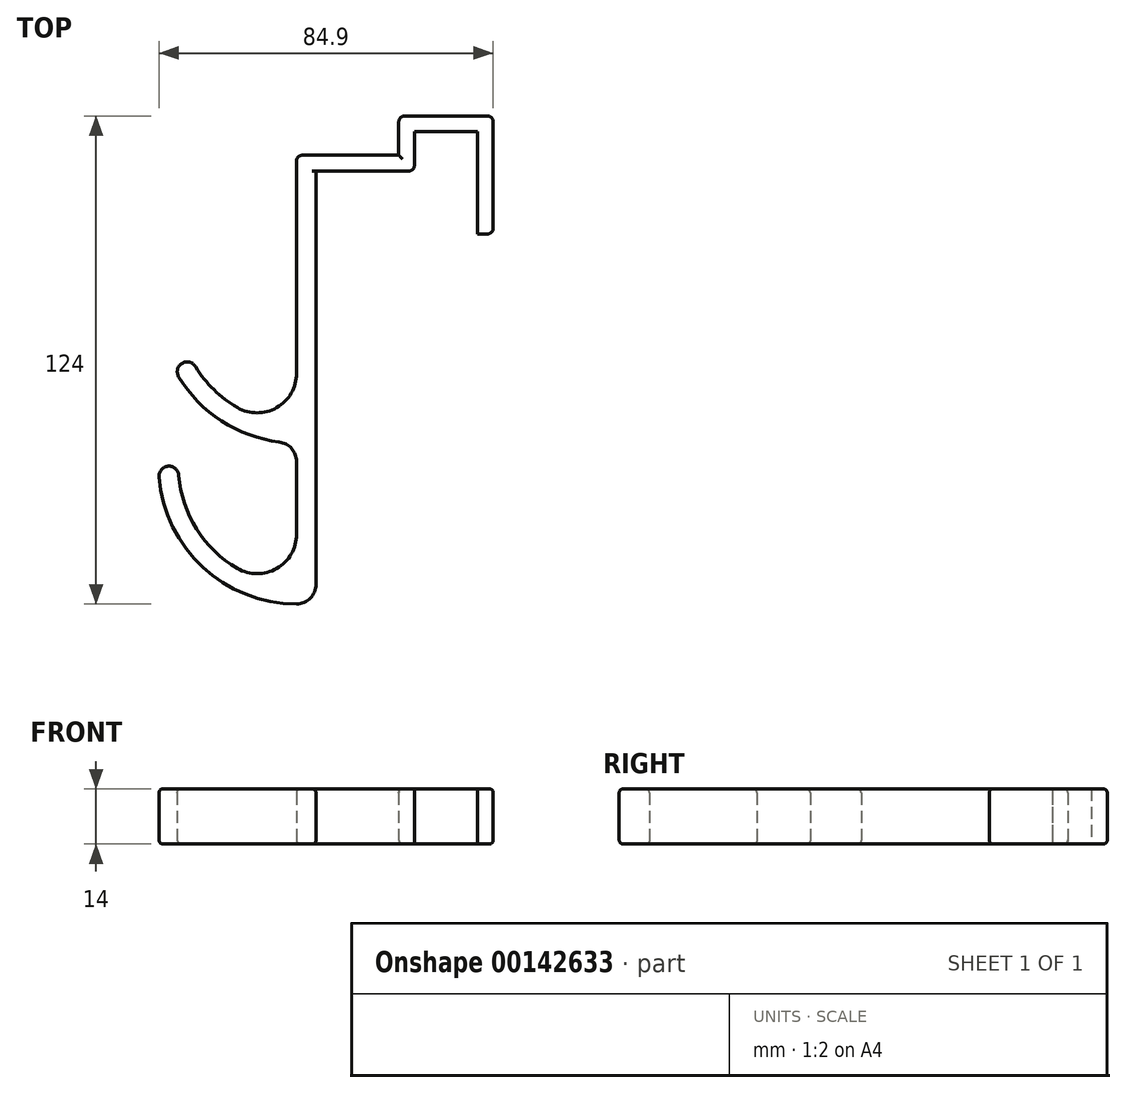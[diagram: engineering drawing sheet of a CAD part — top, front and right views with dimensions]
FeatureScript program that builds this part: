
annotation { "Feature Type Name" : "Feature", "Feature Type Description" : "" }
export const myFeature = defineFeature(function(context is Context, id is Id, definition is map)
    precondition{}
    {
        {
            var Q0;
            Q0=qCreatedBy(makeId("Top.planeOp"),FACE);
            var sketch = newSketch(context, id + "F0", { "sketchPlane" : qUnion([Q0])});
            skLineSegment(sketch, "E0", {"start": v(45, -14.5) * mm, "end": v(45, 12.5) * mm});
            skLineSegment(sketch, "E1", {"start": v(43.5, 14) * mm, "end": v(22.5, 14) * mm});
            skLineSegment(sketch, "E2", {"start": v(21, 12.5) * mm, "end": v(21, 4) * mm});
            skLineSegment(sketch, "E3", {"start": v(21, 4) * mm, "end": v(-3.5, 4) * mm});
            skLineSegment(sketch, "E4", {"start": v(-5, 2.5) * mm, "end": v(-5, -51.45) * mm});
            skLineSegment(sketch, "E5", {"start": v(-37.4, -75) * mm, "end": v(-37.4, -75) * mm});
            skLineSegment(sketch, "E6", {"start": v(-5, -110) * mm, "end": v(-5, -110) * mm});
            skLineSegment(sketch, "E7", {"start": v(0, 0) * mm, "end": v(23.5, 0) * mm});
            skLineSegment(sketch, "E8", {"start": v(25, 1.5) * mm, "end": v(25, 10) * mm});
            skLineSegment(sketch, "E9", {"start": v(25, 10) * mm, "end": v(41, 10) * mm});
            skLineSegment(sketch, "E10", {"start": v(41, 10) * mm, "end": v(41, -16) * mm});
            skLineSegment(sketch, "E11", {"start": v(41, -16) * mm, "end": v(43.5, -16) * mm});
            skLineSegment(sketch, "E12.trimOffspring", {"start": v(0, -105) * mm, "end": v(0, 0) * mm});
            skArc(sketch, "E13", {"start": v(-34.91, -77.3) * mm, "mid": v(-30.38, -90.99) * mm, "end": v(-20, -100.98) * mm});
            skArc(sketch, "E14", {"start": v(-39.9, -77.7) * mm, "mid": v(-28.78, -100.68) * mm, "end": v(-5, -110) * mm});
            skPoint(sketch, "E15.visualSharp", {"position": v(-35, -75) * mm});
            skArc(sketch, "E15.filletArc", {"start": v(-34.91, -77.3) * mm, "mid": v(-35.7, -75.67) * mm, "end": v(-37.4, -75) * mm});
            skPoint(sketch, "E16.visualSharp", {"position": v(-40, -75) * mm});
            skArc(sketch, "E16.filletArc", {"start": v(-37.4, -75) * mm, "mid": v(-39.24, -75.8) * mm, "end": v(-39.9, -77.7) * mm});
            skPoint(sketch, "E17.visualSharp", {"position": v(-5, 4) * mm});
            skArc(sketch, "E17.filletArc", {"start": v(-3.5, 4) * mm, "mid": v(-4.56, 3.56) * mm, "end": v(-5, 2.5) * mm});
            skPoint(sketch, "E18.visualSharp", {"position": v(25, 0) * mm});
            skArc(sketch, "E18.filletArc", {"start": v(23.5, 0) * mm, "mid": v(24.56, 0.44) * mm, "end": v(25, 1.5) * mm});
            skPoint(sketch, "E19.visualSharp", {"position": v(21, 14) * mm});
            skArc(sketch, "E19.filletArc", {"start": v(22.5, 14) * mm, "mid": v(21.44, 13.56) * mm, "end": v(21, 12.5) * mm});
            skPoint(sketch, "E20.visualSharp", {"position": v(45, 14) * mm});
            skArc(sketch, "E20.filletArc", {"start": v(45, 12.5) * mm, "mid": v(44.56, 13.56) * mm, "end": v(43.5, 14) * mm});
            skPoint(sketch, "E21.visualSharp", {"position": v(45, -16) * mm});
            skArc(sketch, "E21.filletArc", {"start": v(43.5, -16) * mm, "mid": v(44.56, -15.56) * mm, "end": v(45, -14.5) * mm});
            skArc(sketch, "E22", {"start": v(-20, -100.98) * mm, "mid": v(-10, -100.98) * mm, "end": v(-5, -92.32) * mm});
            skPoint(sketch, "E23.orphan", {"position": v(-5, -105) * mm});
            skPoint(sketch, "E24.visualSharp", {"position": v(0, -110) * mm});
            skArc(sketch, "E24.filletArc", {"start": v(-5, -110) * mm, "mid": v(-1.46, -108.54) * mm, "end": v(0, -105) * mm});
            skArc(sketch, "E25.0.1.3", {"start": v(-20, -60.11) * mm, "mid": v(-10, -60.11) * mm, "end": v(-5, -51.45) * mm});
            skArc(sketch, "E25.0.1.4", {"start": v(-30.64, -49.71) * mm, "mid": v(-25.97, -55.58) * mm, "end": v(-20, -60.11) * mm});
            skArc(sketch, "E25.0.1.5", {"start": v(-34.91, -52.3) * mm, "mid": v(-24.04, -63.5) * mm, "end": v(-9.37, -68.86) * mm});
            skLineSegment(sketch, "E26.trimOffspring", {"start": v(-5, -73.82) * mm, "end": v(-5, -92.32) * mm});
            skPoint(sketch, "E27.visualSharp", {"position": v(-5, -69.13) * mm});
            skArc(sketch, "E27.filletArc", {"start": v(-5, -73.82) * mm, "mid": v(-6.25, -70.51) * mm, "end": v(-9.38, -68.86) * mm});
            skArc(sketch, "E28", {"start": v(-30.64, -49.71) * mm, "mid": v(-34.07, -48.87) * mm, "end": v(-34.91, -52.3) * mm});
            skLineSegment(sketch, "E29", {"start": v(-34.91, -52.3) * mm, "end": v(-32.77, -51) * mm, "construction": true});
            skLineSegment(sketch, "E30", {"start": v(-32.77, -51) * mm, "end": v(-30.64, -49.71) * mm, "construction": true});
            skLineSegment(sketch, "E31", {"start": v(-34.91, -77.3) * mm, "end": v(-34.91, -52.3) * mm, "construction": true});
            skSolve(sketch);
        }
        {
            var Q0;
            Q0 = qSketchRegion(id + "F0", true);
            extrude(context, id + "F1", {"entities" : qUnion([Q0]), "depth" : 14 * mm});
        }
        {
            var Q0;
            Q0=makeQuery(id+"F1.opExtrude","CAP_EDGE",EDGE,{"disambiguationData":[OSD([sQuery(id+"F0.wireOp",EDGE,"E0")])],"isStart":false});
            var Q1;
            Q1=makeQuery(id+"F1.opExtrude","CAP_EDGE",EDGE,{"disambiguationData":[OSD([sQuery(id+"F0.wireOp",EDGE,"E20.filletArc")])],"isStart":false});
            var Q2;
            Q2=makeQuery(id+"F1.opExtrude","CAP_EDGE",EDGE,{"disambiguationData":[OSD([sQuery(id+"F0.wireOp",EDGE,"E1")])],"isStart":false});
            var Q3;
            Q3=makeQuery(id+"F1.opExtrude","CAP_EDGE",EDGE,{"disambiguationData":[OSD([sQuery(id+"F0.wireOp",EDGE,"E3")])],"isStart":false});
            var Q4;
            Q4=makeQuery(id+"F1.opExtrude","CAP_EDGE",EDGE,{"disambiguationData":[OSD([sQuery(id+"F0.wireOp",EDGE,"E4")])],"isStart":true});
            var Q5;
            Q5=makeQuery(id+"F1.opExtrude","CAP_EDGE",EDGE,{"disambiguationData":[OSD([sQuery(id+"F0.wireOp",EDGE,"E2")])],"isStart":true});
            fillet(context, id + "F2", {"entities" : qUnion([Q0, Q1, Q2, Q3, Q4, Q5]), "radius" : 1 * mm, "tangentPropagation" : true, "allowEdgeOverflow" : false});
        }
    });
